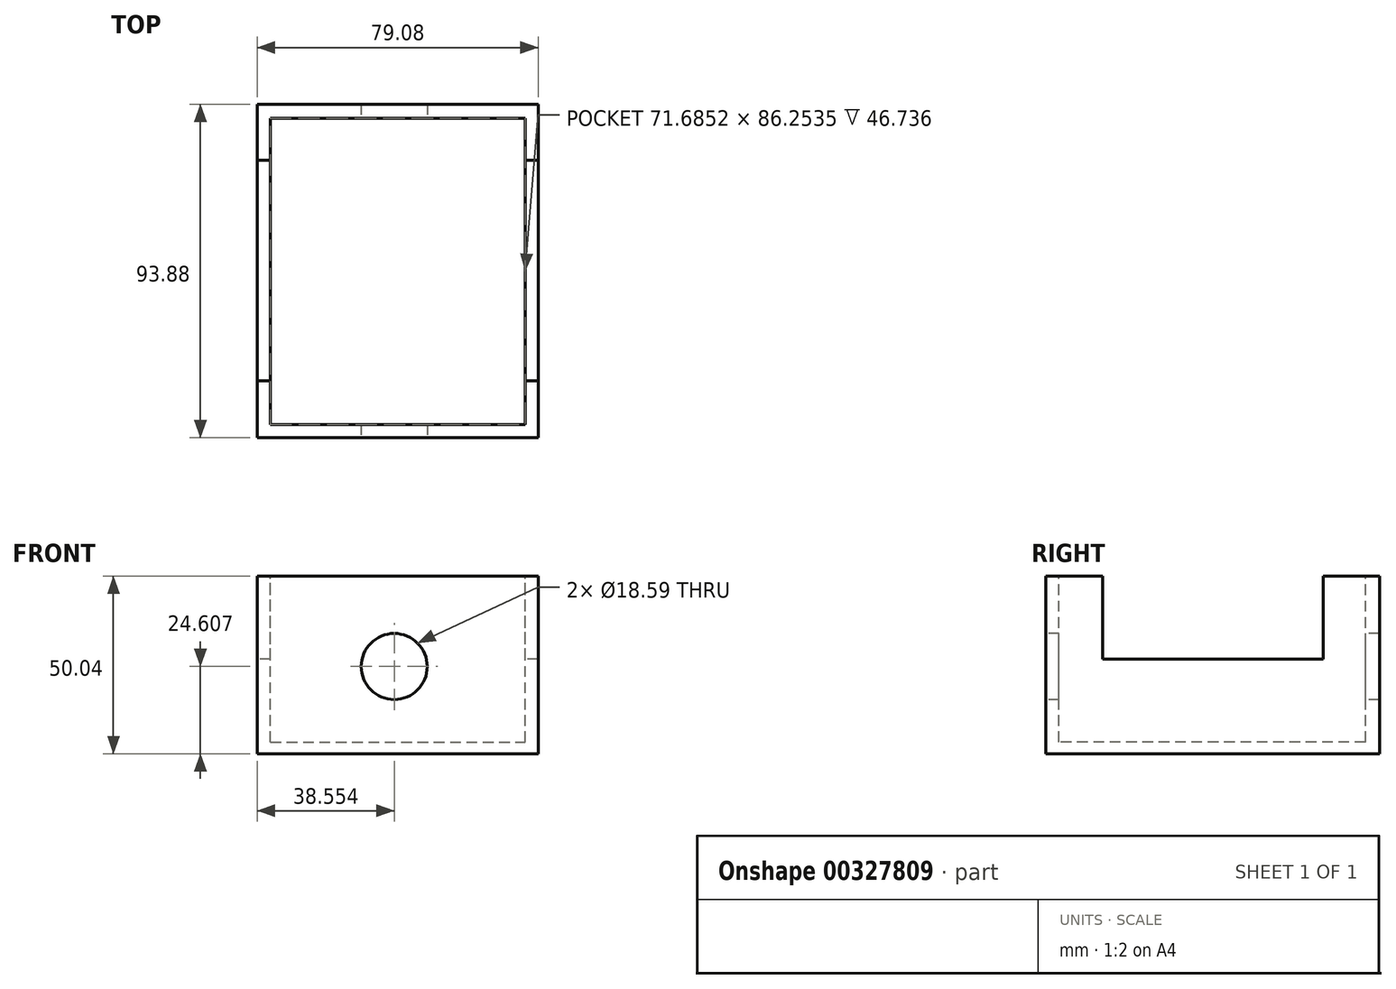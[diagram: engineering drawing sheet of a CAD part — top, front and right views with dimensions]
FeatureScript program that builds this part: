
annotation { "Feature Type Name" : "Feature", "Feature Type Description" : "" }
export const myFeature = defineFeature(function(context is Context, id is Id, definition is map)
    precondition{}
    {
        {
            var Q0;
            Q0=qCreatedBy(makeId("Top.planeOp"),FACE);
            var sketch = newSketch(context, id + "F0", { "sketchPlane" : qUnion([Q0])});
            skLineSegment(sketch, "E0.bottom", {"start": v(-34.22, 46.71) * mm, "end": v(44.86, 46.71) * mm});
            skLineSegment(sketch, "E0.top", {"start": v(-34.22, -47.17) * mm, "end": v(44.86, -47.17) * mm});
            skLineSegment(sketch, "E0.left", {"start": v(-34.22, 46.71) * mm, "end": v(-34.22, -47.17) * mm});
            skLineSegment(sketch, "E0.right", {"start": v(44.86, 46.71) * mm, "end": v(44.86, -47.17) * mm});
            skSolve(sketch);
        }
        {
            var Q0;
            Q0=makeQuery(id+"F0.imprint","IMPRINT",FACE,{"disambiguationData":[TD([[makeQuery(id+"F0.imprint","IMPRINT",EDGE,{"derivedFrom":sQuery(id+"F0.wireOp",EDGE,"E0.bottom")}),-1.0]])]});
            extrude(context, id + "F1", {"entities" : qUnion([Q0]), "depth" : 50.04 * mm});
        }
        {
            var Q0;
            Q0=makeQuery(id+"F1.opExtrude","SWEPT_FACE",FACE,{"disambiguationData":[OSD([sQuery(id+"F0.wireOp",EDGE,"E0.left")])]});
            var sketch = newSketch(context, id + "F2", { "sketchPlane" : qUnion([Q0])});
            skLineSegment(sketch, "E1.bottom", {"start": v(-30.91, 50.04) * mm, "end": v(31.16, 50.04) * mm});
            skLineSegment(sketch, "E1.top", {"start": v(-30.91, 26.7) * mm, "end": v(31.16, 26.7) * mm});
            skLineSegment(sketch, "E1.left", {"start": v(-30.91, 50.04) * mm, "end": v(-30.91, 26.7) * mm});
            skLineSegment(sketch, "E1.right", {"start": v(31.16, 50.04) * mm, "end": v(31.16, 26.7) * mm});
            skSolve(sketch);
        }
        {
            var Q0;
            Q0=makeQuery(id+"F2.imprint","IMPRINT",FACE,{"disambiguationData":[TD([[makeQuery(id+"F2.imprint","IMPRINT",EDGE,{"derivedFrom":sQuery(id+"F2.wireOp",EDGE,"E1.bottom")}),-1.0]])]});
            extrude(context, id + "F3", {"entities" : qUnion([Q0]), "operationType" : NewBodyOperationType.REMOVE, "oppositeDirection" : true, "depth" : 124.46 * mm});
        }
        {
            var Q0;
            {var subQ0=sQuery(id+"F0.wireOp",EDGE,"E0.bottom");var subQ1=sQuery(id+"F0.wireOp",EDGE,"E0.right");var subQ2=sQuery(id+"F0.wireOp",EDGE,"E0.left");Q0=makeQuery(id+"F3.boolean.opBoolean","SPLIT",FACE,{"disambiguationData":[TD([makeQuery(id+"F1.opExtrude","SWEPT_FACE",FACE,{"disambiguationData":[OSD([subQ0])]})])],"derivedFrom":makeQuery(id+"F1.opExtrude","CAP_FACE",FACE,{"disambiguationData":[OSD([subQ0,sQuery(id+"F0.wireOp",EDGE,"E0.top"),subQ2,subQ1])],"isStart":false})});}
            var sketch = newSketch(context, id + "F4", { "sketchPlane" : qUnion([Q0])});
            skLineSegment(sketch, "E2.bottom", {"start": v(-30.52, 42.78) * mm, "end": v(41.16, 42.78) * mm});
            skLineSegment(sketch, "E2.top", {"start": v(-30.52, -43.47) * mm, "end": v(41.16, -43.47) * mm});
            skLineSegment(sketch, "E2.left", {"start": v(-30.52, 42.78) * mm, "end": v(-30.52, -43.47) * mm});
            skLineSegment(sketch, "E2.right", {"start": v(41.16, 42.78) * mm, "end": v(41.16, -43.47) * mm});
            skSolve(sketch);
        }
        {
            var Q0;
            {var subQ0=sQuery(id+"F4.wireOp",EDGE,"E2.bottom");Q0=makeQuery(id+"F4.imprint","IMPRINT",FACE,{"disambiguationData":[TD([[makeQuery(id+"F4.imprint","IMPRINT",EDGE,{"derivedFrom":subQ0}),-1.0]])]});}
            var Q1;
            {var subQ0=sQuery(id+"F4.wireOp",EDGE,"E2.top");Q1=makeQuery(id+"F4.imprint","IMPRINT",FACE,{"disambiguationData":[TD([[makeQuery(id+"F4.imprint","IMPRINT",EDGE,{"derivedFrom":subQ0}),1.0]])]});}
            extrude(context, id + "F5", {"entities" : qUnion([Q0, Q1]), "operationType" : NewBodyOperationType.REMOVE, "oppositeDirection" : true, "depth" : 46.74 * mm});
        }
        {
            var Q0;
            Q0=makeQuery(id+"F1.opExtrude","SWEPT_FACE",FACE,{"disambiguationData":[OSD([sQuery(id+"F0.wireOp",EDGE,"E0.top")])]});
            var sketch = newSketch(context, id + "F6", { "sketchPlane" : qUnion([Q0])});
            skCircle(sketch, "E3", {"center": v(4.33, 24.6) * mm, "radius": 9.3 * mm});
            skSolve(sketch);
        }
        {
            var Q0;
            Q0=makeQuery(id+"F6.imprint","IMPRINT",FACE,{"disambiguationData":[TD([[makeQuery(id+"F6.imprint","IMPRINT",EDGE,{"derivedFrom":sQuery(id+"F6.wireOp",EDGE,"E3")}),1.0]])]});
            extrude(context, id + "F7", {"entities" : qUnion([Q0]), "operationType" : NewBodyOperationType.REMOVE, "oppositeDirection" : true, "depth" : 142 * mm});
        }
    });
